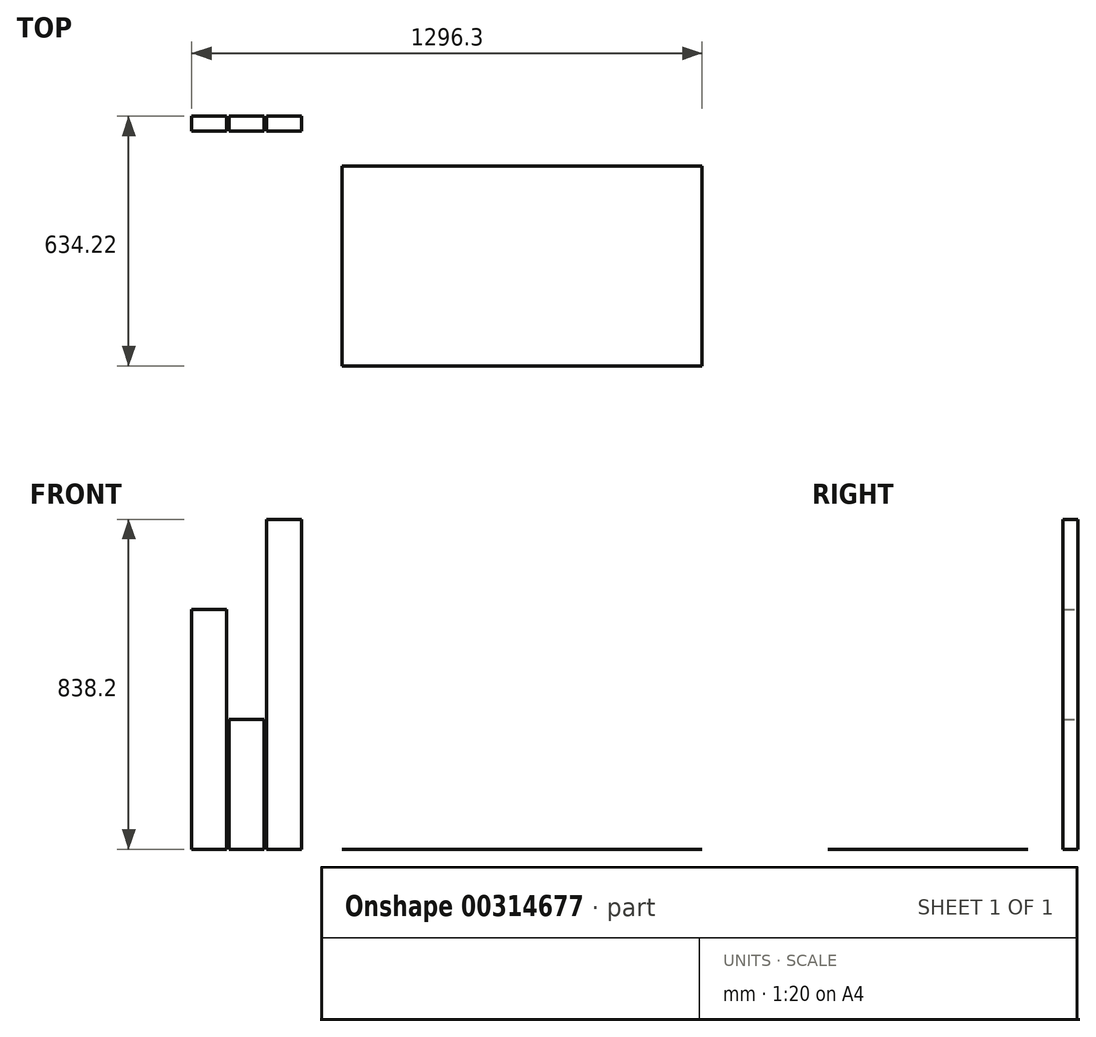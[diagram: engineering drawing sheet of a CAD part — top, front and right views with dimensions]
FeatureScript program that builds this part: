
annotation { "Feature Type Name" : "Feature", "Feature Type Description" : "" }
export const myFeature = defineFeature(function(context is Context, id is Id, definition is map)
    precondition{}
    {
        {
            assignVariable(context, id + "F0", {"name" : "width", "anyValue" : 914.4 * mm});
        }
        {
            assignVariable(context, id + "F1", {"name" : "depth", "anyValue" : 508 * mm});
        }
        {
            assignVariable(context, id + "F2", {"name" : "height", "anyValue" : 609.6 * mm});
        }
        {
            assignVariable(context, id + "F3", {"name" : "top_thickness", "anyValue" : 1 / 101.6 * mm});
        }
        {
            var Q0;
            Q0=qCreatedBy(makeId("Top.planeOp"),FACE);
            var sketch = newSketch(context, id + "F4", { "sketchPlane" : qUnion([Q0])});
            skLineSegment(sketch, "E0.bottom", {"start": v(-81.88, 15.68) * mm, "end": v(-170.78, 15.68) * mm});
            skLineSegment(sketch, "E0.top", {"start": v(-81.88, 53.78) * mm, "end": v(-170.78, 53.78) * mm});
            skLineSegment(sketch, "E0.left", {"start": v(-81.88, 15.68) * mm, "end": v(-81.88, 53.78) * mm});
            skLineSegment(sketch, "E0.right", {"start": v(-170.78, 15.68) * mm, "end": v(-170.78, 53.78) * mm});
            skPoint(sketch, "E0.middle", {"position": v(-126.33, 34.73) * mm});
            skLineSegment(sketch, "E1.bottom", {"start": v(13.37, 15.68) * mm, "end": v(-75.53, 15.68) * mm});
            skLineSegment(sketch, "E1.top", {"start": v(13.37, 53.78) * mm, "end": v(-75.53, 53.78) * mm});
            skLineSegment(sketch, "E1.left", {"start": v(13.37, 15.68) * mm, "end": v(13.37, 53.78) * mm});
            skLineSegment(sketch, "E1.right", {"start": v(-75.53, 15.68) * mm, "end": v(-75.53, 53.78) * mm});
            skPoint(sketch, "E1.middle", {"position": v(-31.08, 34.73) * mm});
            skLineSegment(sketch, "E2.bottom", {"start": v(108.62, 15.68) * mm, "end": v(19.72, 15.68) * mm});
            skLineSegment(sketch, "E2.top", {"start": v(108.62, 53.78) * mm, "end": v(19.72, 53.78) * mm});
            skLineSegment(sketch, "E2.left", {"start": v(108.62, 15.68) * mm, "end": v(108.62, 53.78) * mm});
            skLineSegment(sketch, "E2.right", {"start": v(19.72, 15.68) * mm, "end": v(19.72, 53.78) * mm});
            skPoint(sketch, "E2.middle", {"position": v(64.17, 34.73) * mm});
            skLineSegment(sketch, "E3", {"start": v(-126.33, 34.73) * mm, "end": v(64.17, 34.73) * mm, "construction": true});
            skSolve(sketch);
        }
        {
            var Q0;
            Q0=makeQuery(id+"F4.imprint","IMPRINT",FACE,{"disambiguationData":[TD([[makeQuery(id+"F4.imprint","IMPRINT",EDGE,{"derivedFrom":sQuery(id+"F4.wireOp",EDGE,"E0.bottom")}),-1.0]])]});
            extrude(context, id + "F5", {"entities" : qUnion([Q0]), "depth" : getVariable(context, 'height')});
        }
        {
            var Q0;
            Q0=makeQuery(id+"F4.imprint","IMPRINT",FACE,{"disambiguationData":[TD([[makeQuery(id+"F4.imprint","IMPRINT",EDGE,{"derivedFrom":sQuery(id+"F4.wireOp",EDGE,"E1.bottom")}),-1.0]])]});
            extrude(context, id + "F6", {"entities" : qUnion([Q0]), "depth" : getVariable(context, 'depth') - 88.9 * mm * 2});
        }
        {
            var Q0;
            Q0=makeQuery(id+"F4.imprint","IMPRINT",FACE,{"disambiguationData":[TD([[makeQuery(id+"F4.imprint","IMPRINT",EDGE,{"derivedFrom":sQuery(id+"F4.wireOp",EDGE,"E2.bottom")}),-1.0]])]});
            extrude(context, id + "F7", {"entities" : qUnion([Q0]), "depth" : getVariable(context, 'width') - 38.1 * mm * 2});
        }
        {
            var Q0;
            Q0=qCreatedBy(makeId("Top.planeOp"),FACE);
            var sketch = newSketch(context, id + "F8", { "sketchPlane" : qUnion([Q0])});
            skLineSegment(sketch, "E4.bottom", {"start": v(211.12, -72.44) * mm, "end": v(1125.52, -72.44) * mm});
            skLineSegment(sketch, "E4.top", {"start": v(211.12, -580.44) * mm, "end": v(1125.52, -580.44) * mm});
            skLineSegment(sketch, "E4.left", {"start": v(211.12, -72.44) * mm, "end": v(211.12, -580.44) * mm});
            skLineSegment(sketch, "E4.right", {"start": v(1125.52, -72.44) * mm, "end": v(1125.52, -580.44) * mm});
            skPoint(sketch, "E4.middle", {"position": v(668.32, -326.44) * mm});
            skSolve(sketch);
        }
        {
            var Q0;
            Q0=makeQuery(id+"F8.imprint","IMPRINT",FACE,{"disambiguationData":[TD([[makeQuery(id+"F8.imprint","IMPRINT",EDGE,{"derivedFrom":sQuery(id+"F8.wireOp",EDGE,"E4.bottom")}),-1.0]])]});
            extrude(context, id + "F9", {"entities" : qUnion([Q0]), "depth" : getVariable(context, 'top_thickness')});
        }
    });
